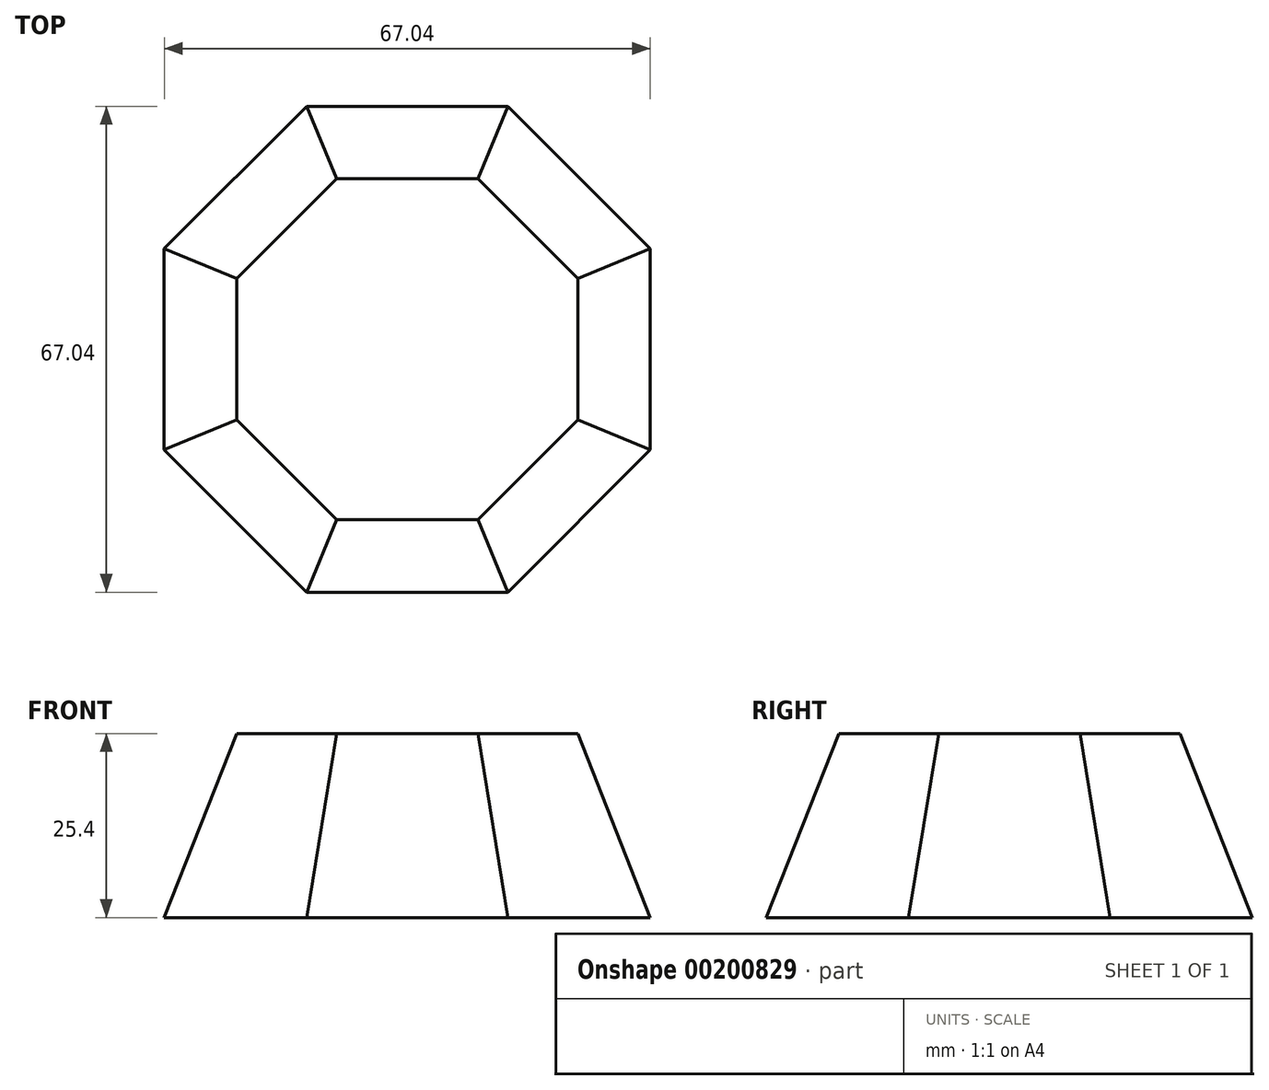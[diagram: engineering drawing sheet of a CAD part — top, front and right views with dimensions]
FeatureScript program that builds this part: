
annotation { "Feature Type Name" : "Feature", "Feature Type Description" : "" }
export const myFeature = defineFeature(function(context is Context, id is Id, definition is map)
    precondition{}
    {
        {
            var Q0;
            Q0=qCreatedBy(makeId("Top.planeOp"),FACE);
            var sketch = newSketch(context, id + "F0", { "sketchPlane" : qUnion([Q0])});
            skCircle(sketch, "E0.cCircle", {"center": v(0, 0) * mm, "radius": 33.52 * mm, "construction": true});
            skLineSegment(sketch, "E0.0", {"start": v(-13.89, 33.52) * mm, "end": v(13.89, 33.52) * mm});
            skLineSegment(sketch, "E0.1", {"start": v(13.89, 33.52) * mm, "end": v(33.52, 13.89) * mm});
            skLineSegment(sketch, "E0.2", {"start": v(33.52, 13.89) * mm, "end": v(33.52, -13.89) * mm});
            skLineSegment(sketch, "E0.3", {"start": v(33.52, -13.89) * mm, "end": v(13.89, -33.52) * mm});
            skLineSegment(sketch, "E0.4", {"start": v(13.89, -33.52) * mm, "end": v(-13.89, -33.52) * mm});
            skLineSegment(sketch, "E0.5", {"start": v(-13.89, -33.52) * mm, "end": v(-33.52, -13.89) * mm});
            skLineSegment(sketch, "E0.6", {"start": v(-33.52, -13.89) * mm, "end": v(-33.52, 13.89) * mm});
            skLineSegment(sketch, "E0.7", {"start": v(-33.52, 13.89) * mm, "end": v(-13.89, 33.52) * mm});
            skPoint(sketch, "E0.0.midPoint", {"position": v(0, 33.52) * mm});
            skSolve(sketch);
        }
        {
            var Q0;
            Q0=qCreatedBy(makeId("Top.planeOp"),FACE);
            cPlane(context, id + "F1", {"entities" : qUnion([Q0]), "cplaneType" : CPlaneType.OFFSET, "offset" : 25.4 * mm, "width" : 152.4 * mm, "height" : 152.4 * mm});
        }
        {
            var Q0;
            Q0=qCreatedBy(id+"F1.planeOp",FACE);
            var sketch = newSketch(context, id + "F2", { "sketchPlane" : qUnion([Q0])});
            skCircle(sketch, "E1.cCircle", {"center": v(0, 0) * mm, "radius": 23.53 * mm, "construction": true});
            skLineSegment(sketch, "E1.0", {"start": v(-9.75, 23.53) * mm, "end": v(9.75, 23.53) * mm});
            skLineSegment(sketch, "E1.1", {"start": v(9.75, 23.53) * mm, "end": v(23.53, 9.75) * mm});
            skLineSegment(sketch, "E1.2", {"start": v(23.53, 9.75) * mm, "end": v(23.53, -9.75) * mm});
            skLineSegment(sketch, "E1.3", {"start": v(23.53, -9.75) * mm, "end": v(9.75, -23.53) * mm});
            skLineSegment(sketch, "E1.4", {"start": v(9.75, -23.53) * mm, "end": v(-9.75, -23.53) * mm});
            skLineSegment(sketch, "E1.5", {"start": v(-9.75, -23.53) * mm, "end": v(-23.53, -9.75) * mm});
            skLineSegment(sketch, "E1.6", {"start": v(-23.53, -9.75) * mm, "end": v(-23.53, 9.75) * mm});
            skLineSegment(sketch, "E1.7", {"start": v(-23.53, 9.75) * mm, "end": v(-9.75, 23.53) * mm});
            skPoint(sketch, "E1.0.midPoint", {"position": v(0, 23.53) * mm});
            skSolve(sketch);
        }
        {
            var Q0;
            Q0=makeQuery(id+"F2.imprint","IMPRINT",FACE,{"disambiguationData":[TD([[makeQuery(id+"F2.imprint","IMPRINT",EDGE,{"derivedFrom":sQuery(id+"F2.wireOp",EDGE,"E1.0")}),-1.0]])]});
            var Q1;
            Q1=makeQuery(id+"F0.imprint","IMPRINT",FACE,{"disambiguationData":[TD([[makeQuery(id+"F0.imprint","IMPRINT",EDGE,{"derivedFrom":sQuery(id+"F0.wireOp",EDGE,"E0.0")}),-1.0]])]});
            loft(context, id + "F3", {"sheetProfilesArray" : [{ "sheetProfileEntities" : qUnion([Q0]) }, { "sheetProfileEntities" : qUnion([Q1]) }]});
        }
    });
